# Revit family: i-PRO-2MP-Outdoor-Compact-Dome-Network-Camera-WV-S35302-F2L1
name_source: partatom
category: Security Devices
units: mm (PartAtom-declared; Revit-internal decimal feet)

## family parameters
Cut with Voids When Loaded = No
Host = Face
Maintain Annotation Orientation = No
OmniClass Number = 23.85.10.14.11
OmniClass Title = Cameras
Part Type = Normal
Room Calculation Point = No
Round Connector Dimension = Use Diameter
Shared = No

## types (2) — shared parameters
Angle Of View = 132
Audio In = Yes
Audio Out = No
Communication Ports = 10Base-T / 100Base-TX, RJ45 connector
Date Last Modified = 2024/03/011
Description = i-PRO, 2MP, Outdoor, Compact Dome, Network Camera, WV-S35302-F2L1
Diameter = 4.291 "
Dome Part Number = WV-CW6SA
EMC = FCC (Part15 ClassA), ICES-003 ClassA, EN55032 ClassA, EN55035
Equipment Abbreviation = SC
Family Version = 1.0.0
HFOV Max 169 = 132.00°
HFOV Max 43 = 99.00°
HFOV Min 169 = 0.00°
HFOV Min 43 = 0.00°
Height = 2.087 "
IP Or Analog = IP
Indoor Or Outdoor = Outdoor
Manufacturer = i-PRO Co., Ltd.
Minimum Illumination = 0 lx
Model = WV-S35302-F2L1
Model Disclaimer = Contact i-PRO for more information
Operational Humidity = 10 to 100 % (no condensation)
Operational Temperature = -20 °C to +50 °C ( -4 °F to 122 °F)
Part Description = i-PRO, 2MP, Outdoor, Compact Dome, Network Camera, WV-S35302-F2L1
Part Number = WV-S35302-F2L1
Product Documentation Link = https://i-pro.com
Product Material = Paint - I-PRO- Black
Product Page URL = https://i-pro.com
Provide Feedback = https://i-pro.com
Satety = UL (UL62368-1), c-UL (CSA C22.2 No.62368-1), CE, IEC62368-1
Shock Resistance = IK10 (IEC 62262)
Storage Temperature = -40 °C to +50 °C ( -22 °F to 122 °F)
URL = https://i-pro.com
VFOV Max 169 = 74.00°
VFOV Max 43 = 74.00°
VFOV Min 169 = 0.00°
VFOV Min 43 = 0.00°
Water and Dust Resistance = IP66 (IEC 60529), Type 4X (UL50E), NEMA 4X compliant
Weight = 1.05 lb
Wind Resistance = Up to 40 m/s {approx. 89 mph}
z Base Radius = 2.146 "
z Camera Resolution Type = 2
z Const Pan Handle Length = 27.559 "
z Const Tilt Base Length = 9.843 "
z Const Tilt Base2 Length = 19.685 "
z Const Tilt Handle Length = 9.843 "
z Const Yaw Base Length = 10.236 "
z Const Yaw Base2 Length = 17.323 "
z Const Yaw Handle Length = 9.252 "
z Dome Material = Acrylic Resin - i-PRO - Clear
z Tilt Offset Length = 0.669 "
z VV Viewpoint Depth Max = 0.689 "
z VV Viewpoint Depth Min = 0.689 "
zero-valued in all types: Default Elevation

## type names (no varying parameters)
- WV-S35302-F2L1 (Wall)
- WV-S35302-F2L1 (Ceiling)

## geometry (parser evidence)
native form markers: Sweep x8
no freeform markers — native parametric forms only
